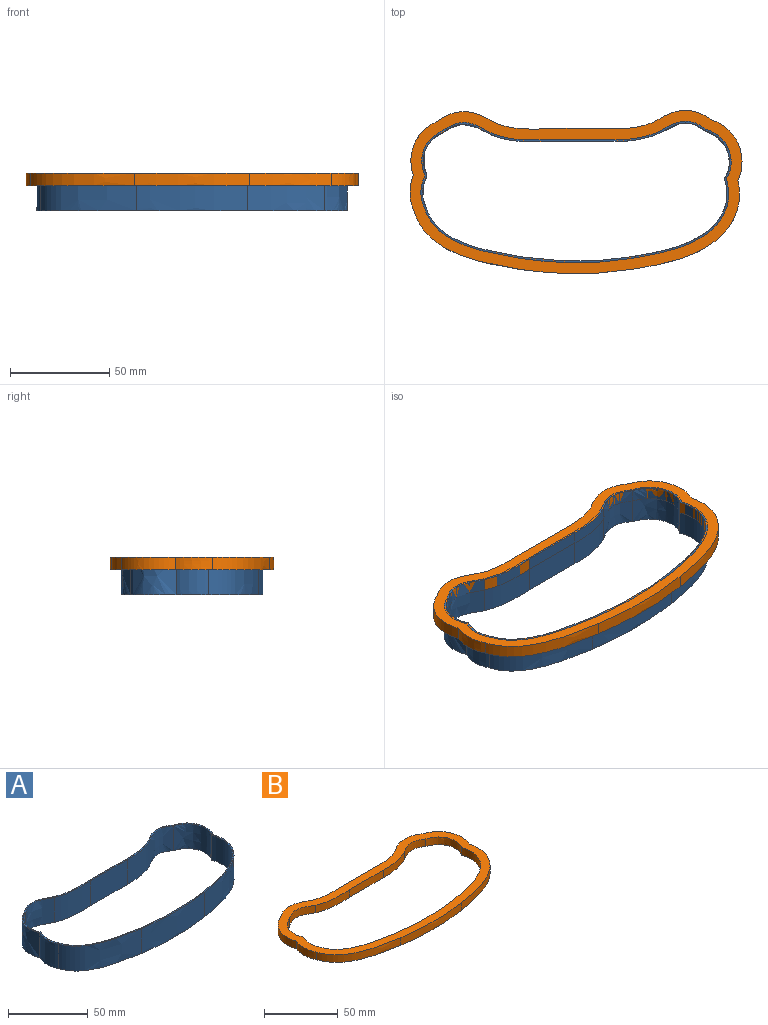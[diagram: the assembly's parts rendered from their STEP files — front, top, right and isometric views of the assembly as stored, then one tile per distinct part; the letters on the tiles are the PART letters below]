
ASSEMBLY  parts=2 mates=1
PART A: 26 faces, bbox 165.1x78.8x26.3 mm
  f0: plane 165.12x78.77mm, normal (0,0,1), area 353.1mm2, adj f2,f3,f4,f5,f6,f7,f8,f9
  f1: plane 165.12x78.77mm, normal (0,0,-1), area 353.1mm2, adj f2,f3,f4,f5,f6,f7,f8,f9
  f2: extruded ~22.82x19.05mm, area 523.6mm2, adj f0,f1,f3,f13
  f3: extruded ~19.05x16.41mm, area 324.9mm2, adj f0,f1,f2,f4
  f4: extruded ~48.17x25.16mm, area 1090.3mm2, adj f0,f1,f3,f5
  f5: extruded ~56.21x19.05mm, area 1075.2mm2, adj f0,f1,f4,f6
  f6: extruded ~38.76x19.05mm, area 787.1mm2, adj f0,f1,f5,f7
  f7: extruded ~27.18x19.05mm, area 583.1mm2, adj f0,f1,f6,f8
  f8: extruded ~25.08x19.05mm, area 601.6mm2, adj f0,f1,f7,f9
  f9: extruded ~22.34x19.05mm, area 463.6mm2, adj f0,f1,f8,f10
  f10: extruded ~24.42x19.05mm, area 478.4mm2, adj f0,f1,f9,f11
  f11: extruded ~32.53x19.05mm, area 619.8mm2, adj f0,f1,f10,f12
  f12: extruded ~28.43x19.05mm, area 549.5mm2, adj f0,f1,f11,f13
  f13: extruded ~24.95x19.05mm, area 517.4mm2, adj f0,f1,f2,f12
  f14: extruded ~22.07x19.05mm, area 506.6mm2, adj f0,f1,f15,f25
  f15: extruded ~19.05x16.04mm, area 318.1mm2, adj f0,f1,f14,f16
  f16: extruded ~47.48x24.61mm, area 1072.9mm2, adj f0,f1,f15,f17
  f17: extruded ~55.92x19.05mm, area 1069.6mm2, adj f0,f1,f16,f18
  f18: extruded ~38.38x19.05mm, area 779.1mm2, adj f0,f1,f17,f19
  f19: extruded ~26.67x19.05mm, area 571.8mm2, adj f0,f1,f18,f20
  f20: extruded ~24.07x19.05mm, area 580.8mm2, adj f0,f1,f19,f21
  f21: extruded ~21.47x19.05mm, area 446.4mm2, adj f0,f1,f20,f22
  f22: extruded ~24.89x19.05mm, area 487.8mm2, adj f0,f1,f21,f23
  f23: extruded ~32.47x19.05mm, area 618.6mm2, adj f0,f1,f22,f24
  f24: extruded ~28.82x19.05mm, area 557.3mm2, adj f0,f1,f23,f25
  f25: extruded ~24.16x19.05mm, area 502mm2, adj f0,f1,f14,f24
PART B: 26 faces, bbox 172.5x87.4x11.4 mm
  f0: plane 172.49x87.39mm, normal (0,0,1), area 2627.7mm2, adj f2,f3,f4,f5,f6,f7,f8,f9
  f1: plane 172.49x87.39mm, normal (0,0,-1), area 2627.7mm2, adj f2,f3,f4,f5,f6,f7,f8,f9
  f2: extruded ~27.42x13.27mm, area 209.4mm2, adj f0,f1,f3,f13
  f3: extruded ~18.68x6.35mm, area 122.2mm2, adj f0,f1,f2,f4
  f4: extruded ~52.4x28.5mm, area 399.2mm2, adj f0,f1,f3,f5
  f5: extruded ~58.03x6.35mm, area 370mm2, adj f0,f1,f4,f6
  f6: extruded ~41.1x14.08mm, area 278.8mm2, adj f0,f1,f5,f7
  f7: extruded ~30.69x12.35mm, area 220.5mm2, adj f0,f1,f6,f8
  f8: extruded ~30.8x15.77mm, area 242.1mm2, adj f0,f1,f7,f9
  f9: extruded ~27.67x6.35mm, area 189.6mm2, adj f0,f1,f8,f10
  f10: extruded ~21.54x6.35mm, area 140.5mm2, adj f0,f1,f9,f11
  f11: extruded ~32.89x6.35mm, area 208.9mm2, adj f0,f1,f10,f12
  f12: extruded ~25.97x6.35mm, area 167.2mm2, adj f0,f1,f11,f13
  f13: extruded ~29.86x6.35mm, area 204.6mm2, adj f0,f1,f2,f12
  f14: extruded ~22.07x10.04mm, area 168.9mm2, adj f0,f1,f15,f25
  f15: extruded ~16.04x6.35mm, area 106mm2, adj f0,f1,f14,f16
  f16: extruded ~47.48x24.61mm, area 357.6mm2, adj f0,f1,f15,f17
  f17: extruded ~55.92x6.35mm, area 356.5mm2, adj f0,f1,f16,f18
  f18: extruded ~38.38x12.88mm, area 259.7mm2, adj f0,f1,f17,f19
  f19: extruded ~26.67x9.85mm, area 190.6mm2, adj f0,f1,f18,f20
  f20: extruded ~24.07x12.42mm, area 193.6mm2, adj f0,f1,f19,f21
  f21: extruded ~21.47x6.35mm, area 148.8mm2, adj f0,f1,f20,f22
  f22: extruded ~24.89x6.35mm, area 162.6mm2, adj f0,f1,f21,f23
  f23: extruded ~32.47x6.35mm, area 206.2mm2, adj f0,f1,f22,f24
  f24: extruded ~28.82x6.35mm, area 185.8mm2, adj f0,f1,f23,f25
  f25: extruded ~24.16x6.35mm, area 167.3mm2, adj f0,f1,f14,f24
PLACE A t=(222.99,12.22,-12.7)mm
PLACE B at identity
MATE fastened A.f0 <-> B.f0  axis (0,0,1) through (156.46,29.15,6.35)mm
